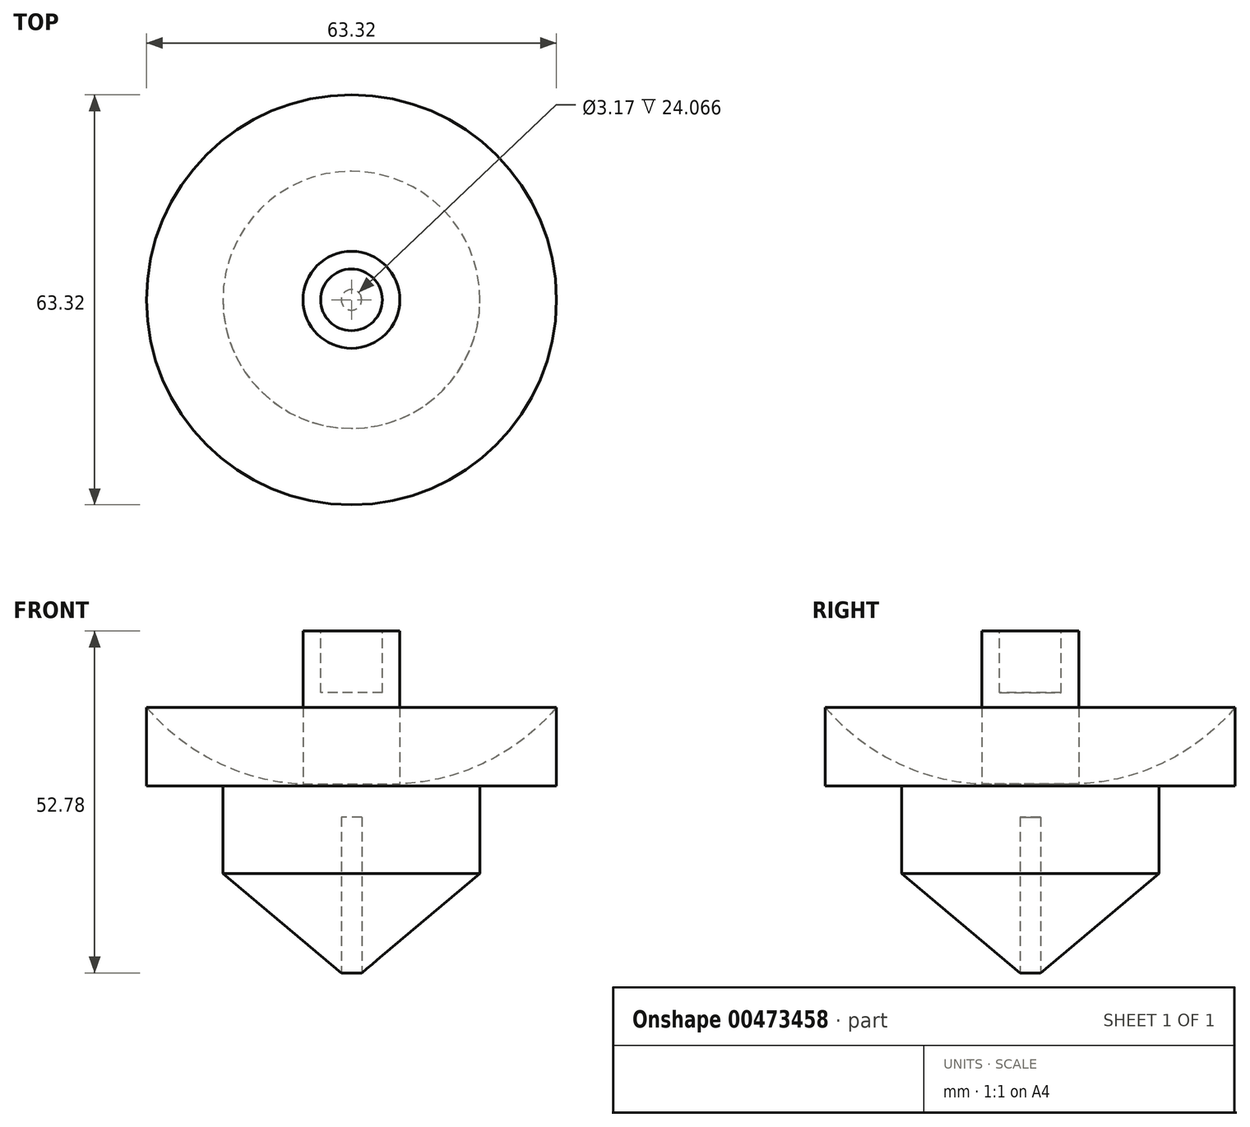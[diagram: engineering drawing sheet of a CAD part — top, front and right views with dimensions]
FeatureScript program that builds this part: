
annotation { "Feature Type Name" : "Feature", "Feature Type Description" : "" }
export const myFeature = defineFeature(function(context is Context, id is Id, definition is map)
    precondition{}
    {
        {
            var Q0;
            Q0=qCreatedBy(makeId("Front.planeOp"),FACE);
            var sketch = newSketch(context, id + "F0", { "sketchPlane" : qUnion([Q0])});
            skLineSegment(sketch, "E0", {"start": v(0, 0) * mm, "end": v(19.86, 16.7) * mm});
            skLineSegment(sketch, "E1", {"start": v(19.86, 16.7) * mm, "end": v(19.86, 30.22) * mm});
            skLineSegment(sketch, "E2", {"start": v(19.86, 30.22) * mm, "end": v(31.66, 30.22) * mm});
            skLineSegment(sketch, "E3", {"start": v(31.66, 30.22) * mm, "end": v(31.66, 42.3) * mm});
            skLineSegment(sketch, "E4", {"start": v(0, 0) * mm, "end": v(0, 54.1) * mm});
            skLineSegment(sketch, "E5", {"start": v(0, 54.1) * mm, "end": v(7.48, 54.1) * mm});
            skLineSegment(sketch, "E6", {"start": v(7.48, 54.1) * mm, "end": v(7.48, 30.5) * mm});
            skArc(sketch, "E7", {"start": v(7.48, 30.5) * mm, "mid": v(20.8, 33.9) * mm, "end": v(31.66, 42.3) * mm});
            skSolve(sketch);
        }
        {
            var Q0;
            Q0=makeQuery(id+"F0.imprint","IMPRINT",FACE,{"disambiguationData":[TD([[makeQuery(id+"F0.imprint","IMPRINT",EDGE,{"derivedFrom":sQuery(id+"F0.wireOp",EDGE,"E0")}),1.0]])]});
            var Q1;
            Q1=sQuery(id+"F0.wireOp",EDGE,"E4");
            revolve(context, id + "F1", {"entities" : qUnion([Q0]), "axis" : qUnion([Q1]), "revolveType" : RevolveType.FULL});
        }
        {
            var Q0;
            Q0=makeQuery(id+"F1.opRevolve","SWEPT_FACE",FACE,{"disambiguationData":[OSD([sQuery(id+"F0.wireOp",EDGE,"E5")])]});
            var sketch = newSketch(context, id + "F2", { "sketchPlane" : qUnion([Q0])});
            skCircle(sketch, "E8", {"center": v(0, 0) * mm, "radius": 4.76 * mm});
            skSolve(sketch);
        }
        {
            var Q0;
            Q0=makeQuery(id+"F2.imprint","IMPRINT",FACE,{"disambiguationData":[TD([[makeQuery(id+"F2.imprint","IMPRINT",EDGE,{"derivedFrom":sQuery(id+"F2.wireOp",EDGE,"E8")}),1.0]])]});
            extrude(context, id + "F3", {"entities" : qUnion([Q0]), "operationType" : NewBodyOperationType.REMOVE, "oppositeDirection" : true, "depth" : 9.52 * mm});
        }
        {
            var Q0;
            Q0=qCreatedBy(makeId("Top.planeOp"),FACE);
            var sketch = newSketch(context, id + "F4", { "sketchPlane" : qUnion([Q0])});
            skCircle(sketch, "E9", {"center": v(0, 0) * mm, "radius": 1.59 * mm});
            skSolve(sketch);
        }
        {
            var Q0;
            Q0=makeQuery(id+"F4.imprint","IMPRINT",FACE,{"disambiguationData":[TD([[makeQuery(id+"F4.imprint","IMPRINT",EDGE,{"derivedFrom":sQuery(id+"F4.wireOp",EDGE,"E9")}),1.0]])]});
            extrude(context, id + "F5", {"entities" : qUnion([Q0]), "operationType" : NewBodyOperationType.REMOVE, "depth" : 25.4 * mm});
        }
    });
